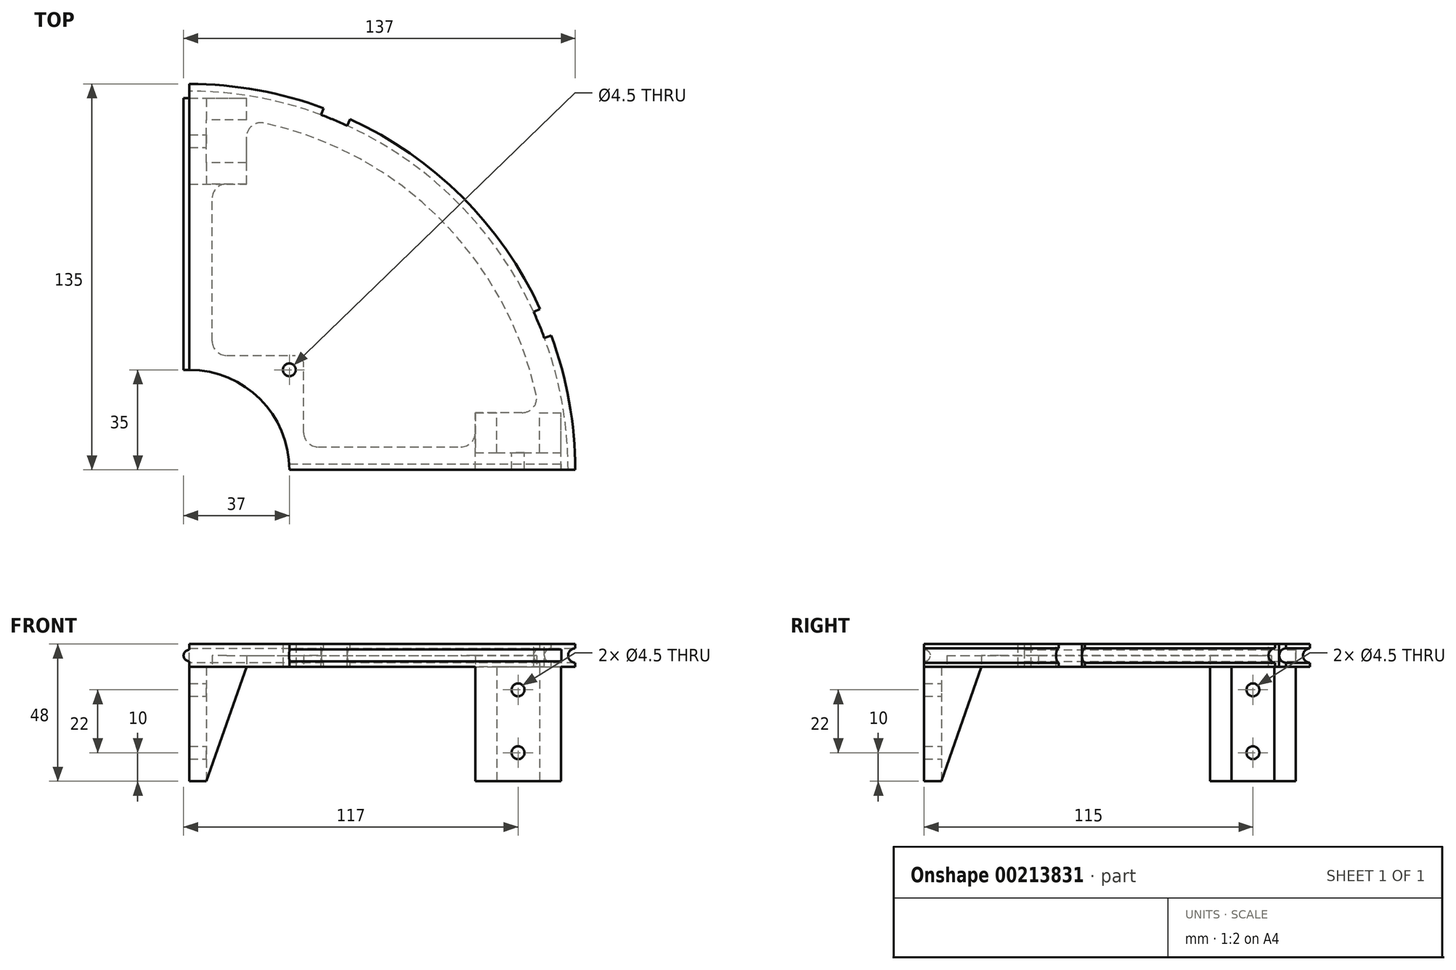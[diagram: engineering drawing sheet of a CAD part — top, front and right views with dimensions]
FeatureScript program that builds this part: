
annotation { "Feature Type Name" : "Feature", "Feature Type Description" : "" }
export const myFeature = defineFeature(function(context is Context, id is Id, definition is map)
    precondition{}
    {
        {
            var Q0;
            Q0=qCreatedBy(makeId("Top.planeOp"),FACE);
            var sketch = newSketch(context, id + "F0", { "sketchPlane" : qUnion([Q0])});
            skArc(sketch, "E0", {"start": v(135, 0) * mm, "mid": v(95.46, 95.46) * mm, "end": v(0, 135) * mm});
            skArc(sketch, "E1", {"start": v(35, 0) * mm, "mid": v(24.75, 24.75) * mm, "end": v(0, 35) * mm});
            skLineSegment(sketch, "E2.trimOffspring", {"start": v(35, 0) * mm, "end": v(135, 0) * mm});
            skLineSegment(sketch, "E3.1.5", {"start": v(0, 35) * mm, "end": v(0, 135) * mm});
            skCircle(sketch, "E4", {"center": v(35, 35) * mm, "radius": 2.25 * mm});
            skSolve(sketch);
        }
        {
            var Q0;
            Q0=qSketchRegion(id+"F0",true);
            extrude(context, id + "F1", {"entities" : qUnion([Q0]), "depth" : 8 * mm});
        }
        {
            var Q0;
            Q0=qCreatedBy(makeId("Top.planeOp"),FACE);
            cPlane(context, id + "F2", {"entities" : qUnion([Q0]), "cplaneType" : CPlaneType.OFFSET, "offset" : 4 * mm, "width" : 150 * mm, "height" : 150 * mm});
        }
        {
            var Q0;
            Q0=qCreatedBy(id+"F2.planeOp",FACE);
            var sketch = newSketch(context, id + "F3", { "sketchPlane" : qUnion([Q0])});
            skCircle(sketch, "E5", {"center": v(0, 0) * mm, "radius": 135 * mm});
            skSolve(sketch);
        }
        {
            var Q0;
            Q0=makeQuery(id+"F1.opExtrude","SWEPT_FACE",FACE,{"disambiguationData":[OSD([sQuery(id+"F0.wireOp",EDGE,"E2.trimOffspring")])]});
            var sketch = newSketch(context, id + "F4", { "sketchPlane" : qUnion([Q0])});
            skCircle(sketch, "E6", {"center": v(135, 4) * mm, "radius": 2.5 * mm});
            skSolve(sketch);
        }
        {
            var Q0;
            Q0=qSketchRegion(id+"F4",true);
            var Q1;
            Q1=qConstructionFilter(qBodyType(qCreatedBy(id+"F3",EDGE),BodyType.WIRE),ConstructionObject.NO);
            sweep(context, id + "F5", {"operationType" : NewBodyOperationType.REMOVE, "profiles" : qUnion([Q0]), "path" : qUnion([Q1])});
        }
        {
            var Q0;
            Q0=makeQuery(id+"F1.opExtrude","CAP_FACE",FACE,{"disambiguationData":[OSD([sQuery(id+"F0.wireOp",EDGE,"E0"),sQuery(id+"F0.wireOp",EDGE,"E1"),sQuery(id+"F0.wireOp",EDGE,"E2.trimOffspring"),sQuery(id+"F0.wireOp",EDGE,"E3.1.5"),sQuery(id+"F0.wireOp",EDGE,"E4")])],"isStart":true});
            var sketch = newSketch(context, id + "F6", { "sketchPlane" : qUnion([Q0])});
            skLineSegment(sketch, "E7.bottom", {"start": v(100, 0) * mm, "end": v(130, 0) * mm});
            skLineSegment(sketch, "E7.top", {"start": v(100, -20) * mm, "end": v(130, -20) * mm});
            skLineSegment(sketch, "E7.left", {"start": v(100, 0) * mm, "end": v(100, -20) * mm});
            skLineSegment(sketch, "E7.right", {"start": v(130, 0) * mm, "end": v(130, -20) * mm});
            skLineSegment(sketch, "E8.bottom", {"start": v(0, -100) * mm, "end": v(20, -100) * mm});
            skLineSegment(sketch, "E8.top", {"start": v(0, -130) * mm, "end": v(20, -130) * mm});
            skLineSegment(sketch, "E8.left", {"start": v(0, -100) * mm, "end": v(0, -130) * mm});
            skLineSegment(sketch, "E8.right", {"start": v(20, -100) * mm, "end": v(20, -130) * mm});
            skSolve(sketch);
        }
        {
            var Q0;
            Q0=qSketchRegion(id+"F6",true);
            extrude(context, id + "F7", {"entities" : qUnion([Q0]), "operationType" : NewBodyOperationType.ADD, "depth" : 40 * mm});
        }
        {
            var Q0;
            Q0=makeQuery(id+"F7.opExtrude","CAP_FACE",FACE,{"disambiguationData":[OSD([sQuery(id+"F6.wireOp",EDGE,"E7.bottom"),sQuery(id+"F6.wireOp",EDGE,"E7.top"),sQuery(id+"F6.wireOp",EDGE,"E7.left"),sQuery(id+"F6.wireOp",EDGE,"E7.right")])],"isStart":false});
            var sketch = newSketch(context, id + "F8", { "sketchPlane" : qUnion([Q0])});
            skLineSegment(sketch, "E9.bottom", {"start": v(107.5, -6) * mm, "end": v(122.5, -6) * mm});
            skLineSegment(sketch, "E9.top", {"start": v(107.5, -20) * mm, "end": v(122.5, -20) * mm});
            skLineSegment(sketch, "E9.left", {"start": v(107.5, -6) * mm, "end": v(107.5, -20) * mm});
            skLineSegment(sketch, "E9.right", {"start": v(122.5, -6) * mm, "end": v(122.5, -20) * mm});
            skLineSegment(sketch, "E10.bottom", {"start": v(20, -107.5) * mm, "end": v(6, -107.5) * mm});
            skLineSegment(sketch, "E10.top", {"start": v(20, -122.5) * mm, "end": v(6, -122.5) * mm});
            skLineSegment(sketch, "E10.left", {"start": v(20, -107.5) * mm, "end": v(20, -122.5) * mm});
            skLineSegment(sketch, "E10.right", {"start": v(6, -107.5) * mm, "end": v(6, -122.5) * mm});
            skSolve(sketch);
        }
        {
            var Q0;
            Q0=qSketchRegion(id+"F8",true);
            extrude(context, id + "F9", {"entities" : qUnion([Q0]), "operationType" : NewBodyOperationType.REMOVE, "oppositeDirection" : true, "depth" : 40 * mm});
        }
        {
            var Q0;
            {var subQ0=sQuery(id+"F6.wireOp",EDGE,"E7.left");var subQ1=sQuery(id+"F6.wireOp",EDGE,"E7.top");Q0=makeQuery(id+"F9.boolean.opBoolean","SPLIT",EDGE,{"disambiguationData":[TD([makeQuery(id+"F7.opExtrude","SWEPT_FACE",FACE,{"disambiguationData":[OSD([subQ0])]})])],"derivedFrom":makeQuery(id+"F7.opExtrude","CAP_EDGE",EDGE,{"disambiguationData":[OSD([subQ1])],"isStart":false})});}
            var Q1;
            {var subQ0=sQuery(id+"F6.wireOp",EDGE,"E7.right");var subQ1=sQuery(id+"F6.wireOp",EDGE,"E7.top");Q1=makeQuery(id+"F9.boolean.opBoolean","SPLIT",EDGE,{"disambiguationData":[TD([makeQuery(id+"F7.opExtrude","SWEPT_FACE",FACE,{"disambiguationData":[OSD([subQ0])]})])],"derivedFrom":makeQuery(id+"F7.opExtrude","CAP_EDGE",EDGE,{"disambiguationData":[OSD([subQ1])],"isStart":false})});}
            chamfer(context, id + "F10", {"entities" : qUnion([Q0, Q1]), "chamferType" : ChamferType.TWO_OFFSETS, "width1" : 14 * mm, "oppositeDirection" : false, "width2" : 40 * mm, "tangentPropagation" : true});
        }
        {
            var Q0;
            Q0=makeQuery(id+"F9.boolean.opBoolean","COPY",FACE,{"derivedFrom":makeQuery(id+"F9.opExtrude","SWEPT_FACE",FACE,{"disambiguationData":[OSD([sQuery(id+"F8.wireOp",EDGE,"E9.bottom")])]})});
            var sketch = newSketch(context, id + "F11", { "sketchPlane" : qUnion([Q0])});
            skCircle(sketch, "E11", {"center": v(-115, -8) * mm, "radius": 2.25 * mm});
            skCircle(sketch, "E12", {"center": v(-115, -30) * mm, "radius": 2.25 * mm});
            skSolve(sketch);
        }
        {
            var Q0;
            Q0=qSketchRegion(id+"F11",true);
            extrude(context, id + "F12", {"entities" : qUnion([Q0]), "operationType" : NewBodyOperationType.REMOVE, "oppositeDirection" : true, "depth" : 25 * mm});
        }
        {
            var Q0;
            {var subQ0=sQuery(id+"F6.wireOp",EDGE,"E8.bottom");var subQ1=sQuery(id+"F6.wireOp",EDGE,"E8.right");Q0=makeQuery(id+"F9.boolean.opBoolean","SPLIT",EDGE,{"disambiguationData":[TD([makeQuery(id+"F7.opExtrude","SWEPT_FACE",FACE,{"disambiguationData":[OSD([subQ0])]})])],"derivedFrom":makeQuery(id+"F7.opExtrude","CAP_EDGE",EDGE,{"disambiguationData":[OSD([subQ1])],"isStart":false})});}
            var Q1;
            {var subQ0=sQuery(id+"F6.wireOp",EDGE,"E8.right");var subQ1=sQuery(id+"F6.wireOp",EDGE,"E8.top");Q1=makeQuery(id+"F9.boolean.opBoolean","SPLIT",EDGE,{"disambiguationData":[TD([makeQuery(id+"F7.opExtrude","SWEPT_FACE",FACE,{"disambiguationData":[OSD([subQ1])]})])],"derivedFrom":makeQuery(id+"F7.opExtrude","CAP_EDGE",EDGE,{"disambiguationData":[OSD([subQ0])],"isStart":false})});}
            chamfer(context, id + "F13", {"entities" : qUnion([Q0, Q1]), "chamferType" : ChamferType.TWO_OFFSETS, "width1" : 40 * mm, "oppositeDirection" : false, "width2" : 14 * mm, "tangentPropagation" : true});
        }
        {
            var Q0;
            Q0=makeQuery(id+"F9.boolean.opBoolean","COPY",FACE,{"derivedFrom":makeQuery(id+"F9.opExtrude","SWEPT_FACE",FACE,{"disambiguationData":[OSD([sQuery(id+"F8.wireOp",EDGE,"E10.right")])]})});
            var sketch = newSketch(context, id + "F14", { "sketchPlane" : qUnion([Q0])});
            skCircle(sketch, "E13", {"center": v(115, -30) * mm, "radius": 2.25 * mm});
            skCircle(sketch, "E14", {"center": v(115, -8) * mm, "radius": 2.25 * mm});
            skSolve(sketch);
        }
        {
            var Q0;
            Q0=qSketchRegion(id+"F14",true);
            extrude(context, id + "F15", {"entities" : qUnion([Q0]), "operationType" : NewBodyOperationType.REMOVE, "oppositeDirection" : true, "depth" : 25 * mm});
        }
        {
            var Q0;
            Q0=makeQuery(id+"F1.opExtrude","CAP_FACE",FACE,{"disambiguationData":[OSD([sQuery(id+"F0.wireOp",EDGE,"E0"),sQuery(id+"F0.wireOp",EDGE,"E1"),sQuery(id+"F0.wireOp",EDGE,"E2.trimOffspring"),sQuery(id+"F0.wireOp",EDGE,"E3.1.5"),sQuery(id+"F0.wireOp",EDGE,"E4")])],"isStart":false});
            var sketch = newSketch(context, id + "F16", { "sketchPlane" : qUnion([Q0])});
            skArc(sketch, "E15", {"start": v(124.2, 46.14) * mm, "mid": v(122.41, 50.71) * mm, "end": v(120.45, 55.2) * mm});
            skArc(sketch, "E16", {"start": v(126.55, 47.01) * mm, "mid": v(124.72, 51.67) * mm, "end": v(122.72, 56.25) * mm});
            skLineSegment(sketch, "E17", {"start": v(0, 0) * mm, "end": v(124.72, 51.66) * mm, "construction": true});
            skLineSegment(sketch, "E18", {"start": v(0, 0) * mm, "end": v(51.66, 124.72) * mm, "construction": true});
            skLineSegment(sketch, "E19", {"start": v(46.13, 124.21) * mm, "end": v(47, 126.55) * mm});
            skLineSegment(sketch, "E20", {"start": v(124.2, 46.14) * mm, "end": v(126.55, 47.01) * mm});
            skLineSegment(sketch, "E21", {"start": v(55.2, 120.45) * mm, "end": v(56.24, 122.73) * mm});
            skLineSegment(sketch, "E22", {"start": v(120.45, 55.2) * mm, "end": v(122.72, 56.25) * mm});
            skArc(sketch, "E23.trimOffspring", {"start": v(56.24, 122.73) * mm, "mid": v(51.66, 124.73) * mm, "end": v(47, 126.55) * mm});
            skArc(sketch, "E24.trimOffspring", {"start": v(55.2, 120.45) * mm, "mid": v(50.7, 122.42) * mm, "end": v(46.13, 124.21) * mm});
            skSolve(sketch);
        }
        {
            var Q0;
            Q0=qSketchRegion(id+"F16",true);
            extrude(context, id + "F17", {"entities" : qUnion([Q0]), "operationType" : NewBodyOperationType.REMOVE, "oppositeDirection" : true, "depth" : 25 * mm});
        }
        {
            var Q0;
            Q0=makeQuery(id+"F7.boolean.opBoolean","MERGE",FACE,{"derivedFrom":[makeQuery(id+"F1.opExtrude","SWEPT_FACE",FACE,{"disambiguationData":[OSD([sQuery(id+"F0.wireOp",EDGE,"E2.trimOffspring")])]}),makeQuery(id+"F7.opExtrude","SWEPT_FACE",FACE,{"disambiguationData":[OSD([sQuery(id+"F6.wireOp",EDGE,"E7.bottom")])]})]});
            var sketch = newSketch(context, id + "F18", { "sketchPlane" : qUnion([Q0])});
            skLineSegment(sketch, "E25", {"start": v(0, 4) * mm, "end": v(130.2, 4) * mm});
            skSolve(sketch);
        }
        {
            var Q0;
            Q0=makeQuery(id+"F7.boolean.opBoolean","MERGE",FACE,{"derivedFrom":[makeQuery(id+"F1.opExtrude","SWEPT_FACE",FACE,{"disambiguationData":[OSD([sQuery(id+"F0.wireOp",EDGE,"E3.1.5")])]}),makeQuery(id+"F7.opExtrude","SWEPT_FACE",FACE,{"disambiguationData":[OSD([sQuery(id+"F6.wireOp",EDGE,"E8.left")])]})]});
            var sketch = newSketch(context, id + "F19", { "sketchPlane" : qUnion([Q0])});
            skLineSegment(sketch, "E26", {"start": v(-130, 4) * mm, "end": v(0, 4) * mm});
            skSolve(sketch);
        }
        {
            var Q0;
            Q0=qCreatedBy(makeId("Front.planeOp"),FACE);
            var sketch = newSketch(context, id + "F20", { "sketchPlane" : qUnion([Q0])});
            skCircle(sketch, "E27", {"center": v(0, 4) * mm, "radius": 2 * mm});
            skSolve(sketch);
        }
        {
            var Q0;
            Q0=makeQuery(id+"F20.imprint","IMPRINT",FACE,{"disambiguationData":[TD([[makeQuery(id+"F20.imprint","IMPRINT",EDGE,{"derivedFrom":sQuery(id+"F20.wireOp",EDGE,"E27")}),1.0]])]});
            var Q1;
            Q1=sQuery(id+"F19.wireOp",EDGE,"E26");
            sweep(context, id + "F21", {"operationType" : NewBodyOperationType.ADD, "profiles" : qUnion([Q0]), "path" : qUnion([Q1])});
        }
        {
            var Q0;
            Q0=makeQuery(id+"F1.opExtrude","CAP_FACE",FACE,{"disambiguationData":[OSD([sQuery(id+"F0.wireOp",EDGE,"E0"),sQuery(id+"F0.wireOp",EDGE,"E1"),sQuery(id+"F0.wireOp",EDGE,"E2.trimOffspring"),sQuery(id+"F0.wireOp",EDGE,"E3.1.5"),sQuery(id+"F0.wireOp",EDGE,"E4")])],"isStart":false});
            var sketch = newSketch(context, id + "F22", { "sketchPlane" : qUnion([Q0])});
            skCircle(sketch, "E28", {"center": v(0, 0) * mm, "radius": 35 * mm});
            skSolve(sketch);
        }
        {
            var Q0;
            {var subQ0=sQuery(id+"F22.wireOp",EDGE,"E28");var subQ1=makeQuery(id+"F22.imprint","INTERSECT",VERTEX,{"derivedFrom":[makeQuery(id+"F1.opExtrude","CAP_EDGE",EDGE,{"disambiguationData":[OSD([sQuery(id+"F0.wireOp",EDGE,"E2.trimOffspring")])],"isStart":false}),subQ0]});Q0=makeQuery(id+"F22.imprint","IMPRINT",FACE,{"disambiguationData":[TD([[makeQuery(id+"F22.imprint","IMPRINT",EDGE,{"disambiguationData":[TD([[subQ1,-1.0]])],"derivedFrom":subQ0}),1.0]])]});}
            extrude(context, id + "F23", {"entities" : qUnion([Q0]), "operationType" : NewBodyOperationType.REMOVE, "endBound" : BoundingType.THROUGH_ALL, "oppositeDirection" : true, "depth" : 25 * mm});
        }
        {
            var Q0;
            Q0=qCreatedBy(makeId("Right.planeOp"),FACE);
            var sketch = newSketch(context, id + "F24", { "sketchPlane" : qUnion([Q0])});
            skCircle(sketch, "E29", {"center": v(0, 4) * mm, "radius": 2.1 * mm});
            skSolve(sketch);
        }
        {
            var Q0;
            Q0=makeQuery(id+"F24.imprint","IMPRINT",FACE,{"disambiguationData":[TD([[makeQuery(id+"F24.imprint","IMPRINT",EDGE,{"derivedFrom":sQuery(id+"F24.wireOp",EDGE,"E29")}),1.0]])]});
            var Q1;
            Q1=sQuery(id+"F18.wireOp",EDGE,"E25");
            sweep(context, id + "F25", {"operationType" : NewBodyOperationType.REMOVE, "profiles" : qUnion([Q0]), "path" : qUnion([Q1])});
        }
        {
            var Q0;
            Q0=makeQuery(id+"F9.boolean.opBoolean","MERGE",FACE,{"derivedFrom":[makeQuery(id+"F1.opExtrude","CAP_FACE",FACE,{"disambiguationData":[OSD([sQuery(id+"F0.wireOp",EDGE,"E0"),sQuery(id+"F0.wireOp",EDGE,"E1"),sQuery(id+"F0.wireOp",EDGE,"E2.trimOffspring"),sQuery(id+"F0.wireOp",EDGE,"E3.1.5"),sQuery(id+"F0.wireOp",EDGE,"E4")])],"isStart":true}),makeQuery(id+"F9.opExtrude","CAP_FACE",FACE,{"disambiguationData":[OSD([sQuery(id+"F8.wireOp",EDGE,"E9.bottom"),sQuery(id+"F8.wireOp",EDGE,"E9.top"),sQuery(id+"F8.wireOp",EDGE,"E9.left"),sQuery(id+"F8.wireOp",EDGE,"E9.right")])],"isStart":false}),makeQuery(id+"F9.opExtrude","CAP_FACE",FACE,{"disambiguationData":[OSD([sQuery(id+"F8.wireOp",EDGE,"E10.bottom"),sQuery(id+"F8.wireOp",EDGE,"E10.top"),sQuery(id+"F8.wireOp",EDGE,"E10.left"),sQuery(id+"F8.wireOp",EDGE,"E10.right")])],"isStart":false})]});
            var sketch = newSketch(context, id + "F26", { "sketchPlane" : qUnion([Q0])});
            skLineSegment(sketch, "E30.top", {"start": v(13, -40) * mm, "end": v(37, -40) * mm});
            skLineSegment(sketch, "E30.right", {"start": v(40, -13) * mm, "end": v(40, -37) * mm});
            skArc(sketch, "E31", {"start": v(20, -122.5) * mm, "mid": v(87.77, -87.77) * mm, "end": v(122.5, -20) * mm});
            skLineSegment(sketch, "E32", {"start": v(122.5, -20) * mm, "end": v(100, -20) * mm});
            skLineSegment(sketch, "E33", {"start": v(20, -122.5) * mm, "end": v(20, -100) * mm});
            skLineSegment(sketch, "E34", {"start": v(8, -45) * mm, "end": v(8, -100) * mm});
            skLineSegment(sketch, "E35", {"start": v(8, -100) * mm, "end": v(20, -100) * mm});
            skLineSegment(sketch, "E36", {"start": v(45, -8) * mm, "end": v(100, -8) * mm});
            skLineSegment(sketch, "E37", {"start": v(100, -8) * mm, "end": v(100, -20) * mm});
            skPoint(sketch, "E38.visualSharp", {"position": v(40, -40) * mm});
            skArc(sketch, "E38.filletArc", {"start": v(37, -40) * mm, "mid": v(39.12, -39.12) * mm, "end": v(40, -37) * mm});
            skArc(sketch, "E39.filletArc", {"start": v(13, -40) * mm, "mid": v(9.46, -41.46) * mm, "end": v(8, -45) * mm});
            skArc(sketch, "E40.filletArc", {"start": v(45, -8) * mm, "mid": v(41.46, -9.46) * mm, "end": v(40, -13) * mm});
            skSolve(sketch);
        }
        {
            var Q0;
            Q0=qSketchRegion(id+"F26",true);
            extrude(context, id + "F27", {"entities" : qUnion([Q0]), "operationType" : NewBodyOperationType.REMOVE, "oppositeDirection" : true, "depth" : 4 * mm});
        }
        {
            var Q0;
            Q0=makeQuery(id+"F27.boolean.opBoolean","COPY",EDGE,{"derivedFrom":makeQuery(id+"F27.opExtrude","SWEPT_EDGE",EDGE,{"disambiguationData":[OSD([sQuery(id+"F6.wireOp",EDGE,"E7.left"),sQuery(id+"F26.wireOp",EDGE,"E36"),sQuery(id+"F26.wireOp",EDGE,"E37")])]})});
            var Q1;
            Q1=makeQuery(id+"F27.boolean.opBoolean","COPY",EDGE,{"derivedFrom":makeQuery(id+"F27.opExtrude","SWEPT_EDGE",EDGE,{"disambiguationData":[OSD([sQuery(id+"F6.wireOp",EDGE,"E8.bottom"),sQuery(id+"F26.wireOp",EDGE,"E34"),sQuery(id+"F26.wireOp",EDGE,"E35")])]})});
            var Q2;
            Q2=makeQuery(id+"F27.boolean.opBoolean","COPY",EDGE,{"derivedFrom":makeQuery(id+"F27.opExtrude","SWEPT_EDGE",EDGE,{"disambiguationData":[OSD([sQuery(id+"F0.wireOp",EDGE,"E0"),sQuery(id+"F0.wireOp",EDGE,"E1"),sQuery(id+"F0.wireOp",EDGE,"E2.trimOffspring"),sQuery(id+"F0.wireOp",EDGE,"E3.1.5"),sQuery(id+"F0.wireOp",EDGE,"E4"),sQuery(id+"F6.wireOp",EDGE,"E8.right"),sQuery(id+"F8.wireOp",EDGE,"E9.bottom"),sQuery(id+"F8.wireOp",EDGE,"E9.top"),sQuery(id+"F8.wireOp",EDGE,"E9.left"),sQuery(id+"F8.wireOp",EDGE,"E9.right"),sQuery(id+"F8.wireOp",EDGE,"E10.bottom"),sQuery(id+"F8.wireOp",EDGE,"E10.top"),sQuery(id+"F8.wireOp",EDGE,"E10.left"),sQuery(id+"F8.wireOp",EDGE,"E10.right"),sQuery(id+"F26.wireOp",EDGE,"E31"),sQuery(id+"F26.wireOp",EDGE,"E33")])]})});
            var Q3;
            Q3=makeQuery(id+"F27.boolean.opBoolean","COPY",EDGE,{"derivedFrom":makeQuery(id+"F27.opExtrude","SWEPT_EDGE",EDGE,{"disambiguationData":[OSD([sQuery(id+"F0.wireOp",EDGE,"E0"),sQuery(id+"F0.wireOp",EDGE,"E1"),sQuery(id+"F0.wireOp",EDGE,"E2.trimOffspring"),sQuery(id+"F0.wireOp",EDGE,"E3.1.5"),sQuery(id+"F0.wireOp",EDGE,"E4"),sQuery(id+"F6.wireOp",EDGE,"E7.top"),sQuery(id+"F8.wireOp",EDGE,"E9.bottom"),sQuery(id+"F8.wireOp",EDGE,"E9.top"),sQuery(id+"F8.wireOp",EDGE,"E9.left"),sQuery(id+"F8.wireOp",EDGE,"E9.right"),sQuery(id+"F8.wireOp",EDGE,"E10.bottom"),sQuery(id+"F8.wireOp",EDGE,"E10.top"),sQuery(id+"F8.wireOp",EDGE,"E10.left"),sQuery(id+"F8.wireOp",EDGE,"E10.right"),sQuery(id+"F26.wireOp",EDGE,"E31"),sQuery(id+"F26.wireOp",EDGE,"E32")])]})});
            fillet(context, id + "F28", {"entities" : qUnion([Q0, Q1, Q2, Q3]), "radius" : 5 * mm, "tangentPropagation" : true, "allowEdgeOverflow" : false});
        }
    });
